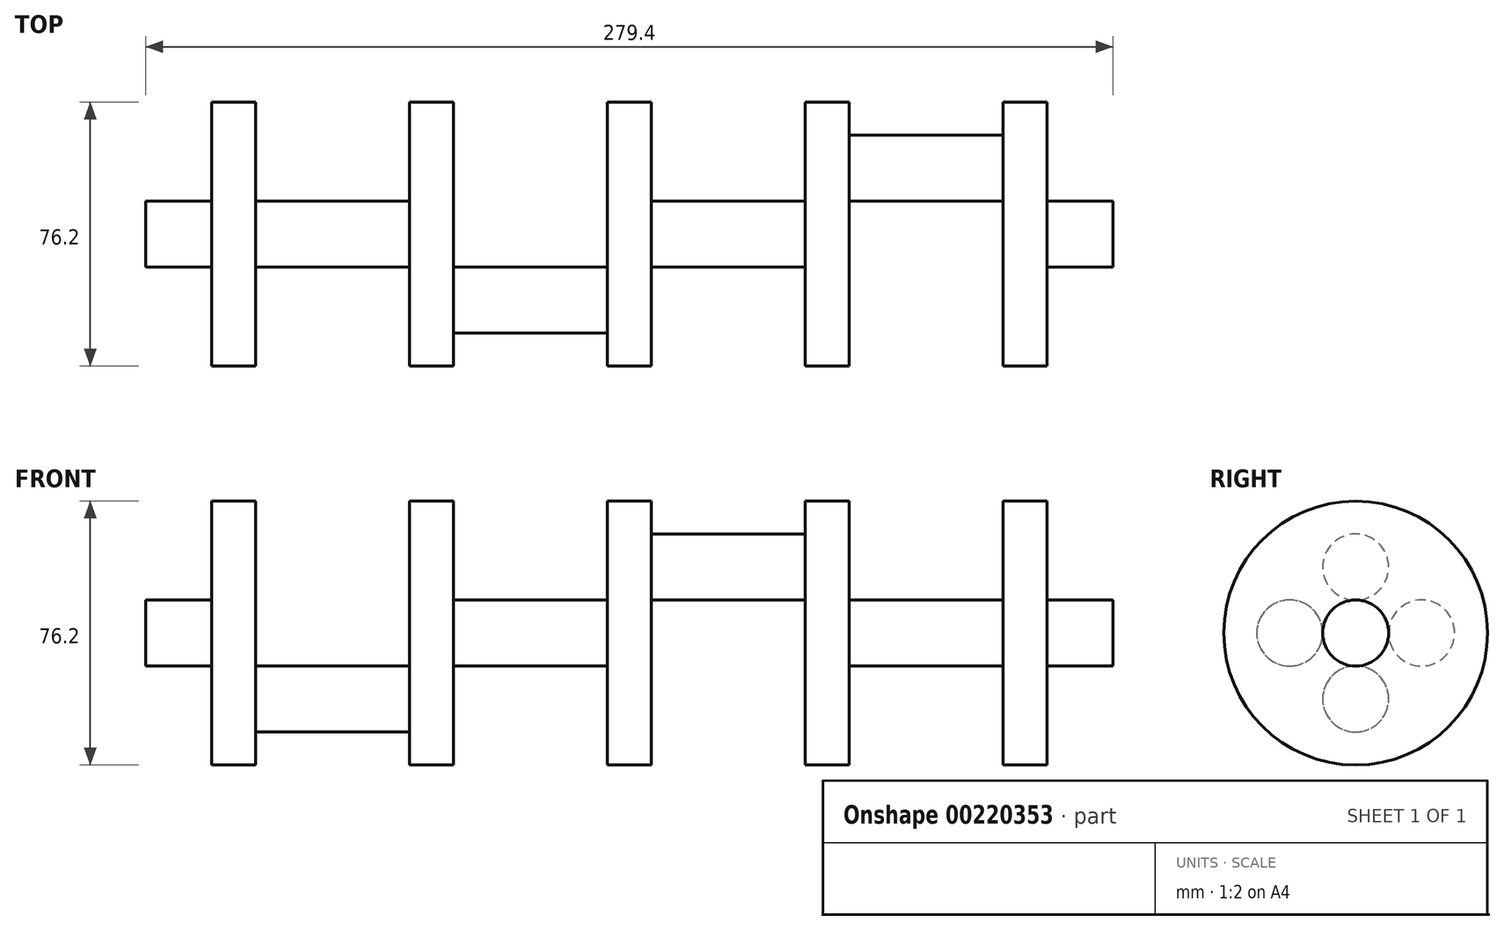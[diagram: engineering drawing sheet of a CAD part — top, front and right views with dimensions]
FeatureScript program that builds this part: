
annotation { "Feature Type Name" : "Feature", "Feature Type Description" : "" }
export const myFeature = defineFeature(function(context is Context, id is Id, definition is map)
    precondition{}
    {
        {
            var Q0;
            Q0=qCreatedBy(makeId("Front.planeOp"),FACE);
            var sketch = newSketch(context, id + "F0", { "sketchPlane" : qUnion([Q0])});
            skLineSegment(sketch, "E0", {"start": v(-139.7, 0) * mm, "end": v(-139.7, -9.52) * mm});
            skLineSegment(sketch, "E1", {"start": v(-139.7, -9.53) * mm, "end": v(-120.65, -9.53) * mm});
            skLineSegment(sketch, "E2", {"start": v(-127, 0) * mm, "end": v(155.37, 0) * mm, "construction": true});
            skPoint(sketch, "E2.startSnap0", {"position": v(-139.7, 0) * mm});
            skLineSegment(sketch, "E3", {"start": v(-120.65, -9.53) * mm, "end": v(-120.65, -38.1) * mm});
            skLineSegment(sketch, "E4", {"start": v(-120.65, -38.1) * mm, "end": v(-107.95, -38.1) * mm});
            skLineSegment(sketch, "E5", {"start": v(-107.95, -38.1) * mm, "end": v(-107.95, 0) * mm});
            skLineSegment(sketch, "E6", {"start": v(-63.5, 0) * mm, "end": v(-63.5, -38.1) * mm});
            skLineSegment(sketch, "E7", {"start": v(-63.5, -38.1) * mm, "end": v(-50.8, -38.1) * mm});
            skLineSegment(sketch, "E8", {"start": v(-50.8, -38.1) * mm, "end": v(-50.8, 0) * mm});
            skLineSegment(sketch, "E9", {"start": v(-50.8, 0) * mm, "end": v(-63.5, 0) * mm});
            skLineSegment(sketch, "E10", {"start": v(-6.35, 0) * mm, "end": v(-6.35, -38.1) * mm});
            skLineSegment(sketch, "E11", {"start": v(-6.35, -38.1) * mm, "end": v(0, -38.1) * mm});
            skLineSegment(sketch, "E12", {"start": v(0, -38.1) * mm, "end": v(0, 0) * mm});
            skLineSegment(sketch, "E13", {"start": v(0, 0) * mm, "end": v(-6.35, 0) * mm});
            skLineSegment(sketch, "E14", {"start": v(-139.7, 0) * mm, "end": v(-107.95, 0) * mm});
            skLineSegment(sketch, "E15.MirrorCS", {"start": v(127, 0) * mm, "end": v(-155.37, 0) * mm, "construction": true});
            skLineSegment(sketch, "E16.MirrorCS", {"start": v(6.35, 0) * mm, "end": v(6.35, -38.1) * mm});
            skLineSegment(sketch, "E17.MirrorCS", {"start": v(6.35, -38.1) * mm, "end": v(0, -38.1) * mm});
            skLineSegment(sketch, "E18.MirrorCS", {"start": v(50.8, -38.1) * mm, "end": v(50.8, 0) * mm});
            skLineSegment(sketch, "E19.MirrorCS", {"start": v(63.5, -38.1) * mm, "end": v(50.8, -38.1) * mm});
            skLineSegment(sketch, "E20.MirrorCS", {"start": v(63.5, 0) * mm, "end": v(63.5, -38.1) * mm});
            skLineSegment(sketch, "E21.MirrorCS", {"start": v(107.95, -38.1) * mm, "end": v(107.95, 0) * mm});
            skLineSegment(sketch, "E22.MirrorCS", {"start": v(120.65, -38.1) * mm, "end": v(107.95, -38.1) * mm});
            skLineSegment(sketch, "E23.MirrorCS", {"start": v(120.65, -9.53) * mm, "end": v(120.65, -38.1) * mm});
            skLineSegment(sketch, "E24.MirrorCS", {"start": v(139.7, -9.53) * mm, "end": v(120.65, -9.53) * mm});
            skLineSegment(sketch, "E25.MirrorCS", {"start": v(139.7, 0) * mm, "end": v(139.7, -9.52) * mm});
            skLineSegment(sketch, "E26", {"start": v(-6.35, 0) * mm, "end": v(6.35, 0) * mm});
            skLineSegment(sketch, "E27", {"start": v(50.8, 0) * mm, "end": v(63.5, 0) * mm});
            skLineSegment(sketch, "E28", {"start": v(107.95, 0) * mm, "end": v(155.37, 0) * mm});
            skSolve(sketch);
        }
        {
            var Q0;
            Q0 = qSketchRegion(id + "F0", true);
            var Q1;
            Q1=sQuery(id+"F0.wireOp",EDGE,"E2");
            revolve(context, id + "F1", {"entities" : qUnion([Q0]), "axis" : qUnion([Q1]), "revolveType" : RevolveType.FULL});
        }
        {
            var Q0;
            Q0=makeQuery(id+"F1.opRevolve","SWEPT_FACE",FACE,{"disambiguationData":[OSD([sQuery(id+"F0.wireOp",EDGE,"E5")])]});
            var sketch = newSketch(context, id + "F2", { "sketchPlane" : qUnion([Q0])});
            skCircle(sketch, "E29", {"center": v(0, 19.05) * mm, "radius": 9.53 * mm});
            skCircle(sketch, "E30", {"center": v(-19.05, 0) * mm, "radius": 9.53 * mm});
            skCircle(sketch, "E31", {"center": v(0, 0) * mm, "radius": 19.05 * mm, "construction": true});
            skCircle(sketch, "E32", {"center": v(0, -19.05) * mm, "radius": 9.53 * mm});
            skCircle(sketch, "E33", {"center": v(19.05, 0) * mm, "radius": 9.53 * mm});
            skSolve(sketch);
        }
        {
            var Q0;
            Q0=makeQuery(id+"F2.imprint","IMPRINT",FACE,{"disambiguationData":[TD([[makeQuery(id+"F2.imprint","IMPRINT",EDGE,{"derivedFrom":sQuery(id+"F2.wireOp",EDGE,"E32")}),1.0]])]});
            var Q1;
            Q1=makeQuery(id+"F1.opRevolve","SWEPT_FACE",FACE,{"disambiguationData":[OSD([sQuery(id+"F0.wireOp",EDGE,"E6")])]});
            extrude(context, id + "F3", {"entities" : qUnion([Q0]), "operationType" : NewBodyOperationType.ADD, "endBound" : BoundingType.UP_TO_SURFACE, "endBoundEntityFace" : qUnion([Q1]), "depth" : 25.4 * mm});
        }
        {
            var Q0;
            Q0=makeQuery(id+"F1.opRevolve","SWEPT_FACE",FACE,{"disambiguationData":[OSD([sQuery(id+"F0.wireOp",EDGE,"E8")])]});
            var sketch = newSketch(context, id + "F4", { "sketchPlane" : qUnion([Q0])});
            skCircle(sketch, "E34.0", {"center": v(-19.05, 0) * mm, "radius": 9.53 * mm});
            skSolve(sketch);
        }
        {
            var Q0;
            Q0 = qSketchRegion(id + "F4", true);
            var Q1;
            Q1=makeQuery(id+"F1.opRevolve","SWEPT_FACE",FACE,{"disambiguationData":[OSD([sQuery(id+"F0.wireOp",EDGE,"E10")])]});
            extrude(context, id + "F5", {"entities" : qUnion([Q0]), "operationType" : NewBodyOperationType.ADD, "endBound" : BoundingType.UP_TO_SURFACE, "endBoundEntityFace" : qUnion([Q1]), "depth" : 25.4 * mm});
        }
        {
            var Q0;
            Q0=makeQuery(id+"F1.opRevolve","SWEPT_FACE",FACE,{"disambiguationData":[OSD([sQuery(id+"F0.wireOp",EDGE,"E16.MirrorCS")])]});
            var sketch = newSketch(context, id + "F6", { "sketchPlane" : qUnion([Q0])});
            skCircle(sketch, "E35.0", {"center": v(0, 19.05) * mm, "radius": 9.53 * mm});
            skSolve(sketch);
        }
        {
            var Q0;
            Q0 = qSketchRegion(id + "F6", true);
            var Q1;
            Q1=makeQuery(id+"F1.opRevolve","SWEPT_FACE",FACE,{"disambiguationData":[OSD([sQuery(id+"F0.wireOp",EDGE,"E18.MirrorCS")])]});
            extrude(context, id + "F7", {"entities" : qUnion([Q0]), "operationType" : NewBodyOperationType.ADD, "endBound" : BoundingType.UP_TO_SURFACE, "endBoundEntityFace" : qUnion([Q1]), "depth" : 25.4 * mm});
        }
        {
            var Q0;
            Q0=makeQuery(id+"F1.opRevolve","SWEPT_FACE",FACE,{"disambiguationData":[OSD([sQuery(id+"F0.wireOp",EDGE,"E20.MirrorCS")])]});
            var sketch = newSketch(context, id + "F8", { "sketchPlane" : qUnion([Q0])});
            skCircle(sketch, "E36.0", {"center": v(19.05, 0) * mm, "radius": 9.53 * mm});
            skSolve(sketch);
        }
        {
            var Q0;
            Q0 = qSketchRegion(id + "F8", true);
            extrude(context, id + "F9", {"entities" : qUnion([Q0]), "operationType" : NewBodyOperationType.ADD, "endBound" : BoundingType.UP_TO_NEXT, "depth" : 25.4 * mm});
        }
    });
